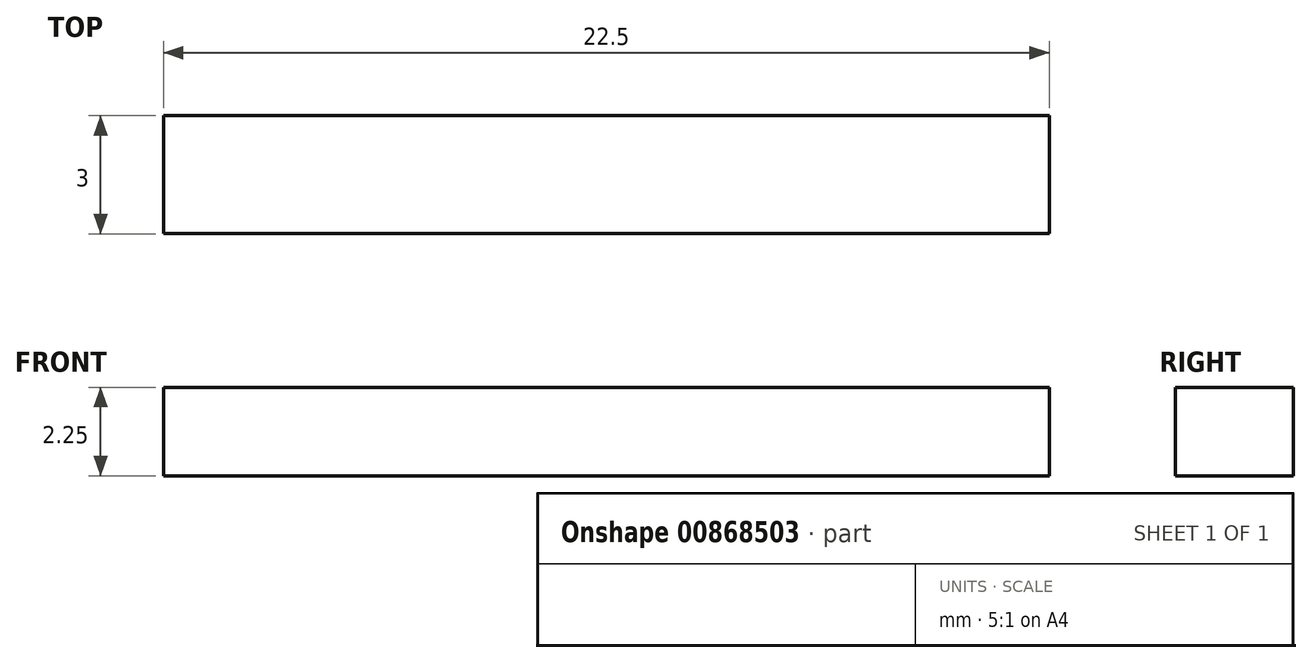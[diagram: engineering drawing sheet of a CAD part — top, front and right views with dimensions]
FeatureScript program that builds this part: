
annotation { "Feature Type Name" : "Feature", "Feature Type Description" : "" }
export const myFeature = defineFeature(function(context is Context, id is Id, definition is map)
    precondition{}
    {
        {
            var Q0;
            Q0=qCreatedBy(makeId("Top.planeOp"),FACE);
            var sketch = newSketch(context, id + "F0", { "sketchPlane" : qUnion([Q0])});
            skLineSegment(sketch, "E0.bottom", {"start": v(-6.14, 2.22) * mm, "end": v(16.36, 2.22) * mm});
            skLineSegment(sketch, "E0.top", {"start": v(-6.14, -0.78) * mm, "end": v(16.36, -0.78) * mm});
            skLineSegment(sketch, "E0.left", {"start": v(-6.14, 2.22) * mm, "end": v(-6.14, -0.78) * mm});
            skLineSegment(sketch, "E0.right", {"start": v(16.36, 2.22) * mm, "end": v(16.36, -0.78) * mm});
            skSolve(sketch);
        }
        {
            var Q0;
            Q0 = qSketchRegion(id + "F0", true);
            extrude(context, id + "F1", {"entities" : qUnion([Q0]), "depth" : 2.25 * mm, "offsetDistance" : 25 * mm});
        }
    });
